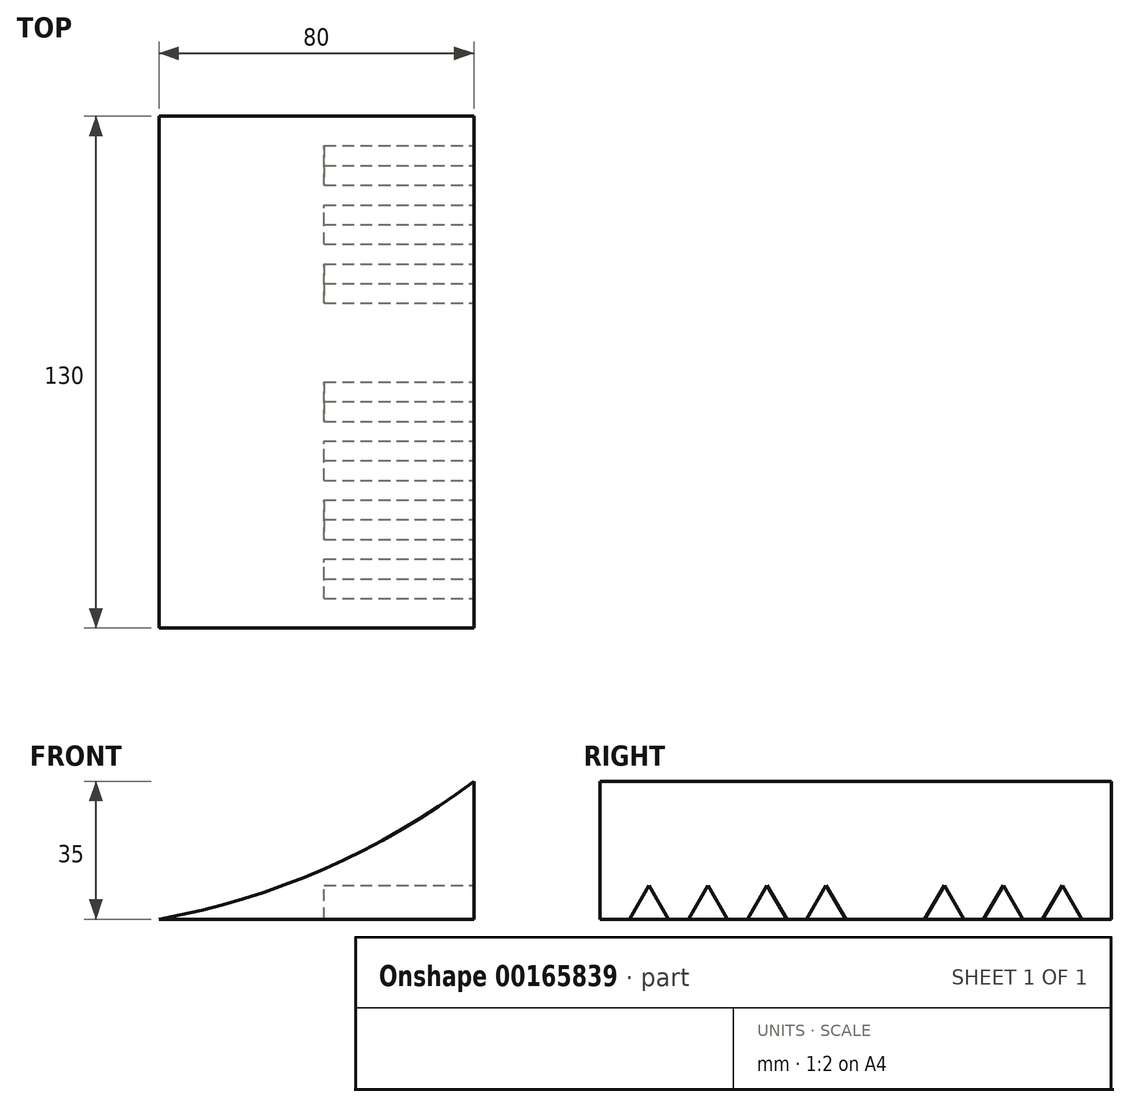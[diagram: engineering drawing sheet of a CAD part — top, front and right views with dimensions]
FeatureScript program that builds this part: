
annotation { "Feature Type Name" : "Feature", "Feature Type Description" : "" }
export const myFeature = defineFeature(function(context is Context, id is Id, definition is map)
    precondition{}
    {
        {
            var Q0;
            Q0=qCreatedBy(makeId("Front.planeOp"),FACE);
            var sketch = newSketch(context, id + "F0", { "sketchPlane" : qUnion([Q0])});
            skLineSegment(sketch, "E0", {"start": v(-40.37, -31.55) * mm, "end": v(39.63, -31.55) * mm});
            skLineSegment(sketch, "E1", {"start": v(39.63, -31.55) * mm, "end": v(39.63, 3.45) * mm});
            skArc(sketch, "E2", {"start": v(-40.37, -31.55) * mm, "mid": v(1.68, -18.73) * mm, "end": v(39.63, 3.45) * mm});
            skSolve(sketch);
        }
        {
            var Q0;
            Q0=makeQuery(id+"F0.imprint","IMPRINT",FACE,{"disambiguationData":[TD([[makeQuery(id+"F0.imprint","IMPRINT",EDGE,{"derivedFrom":sQuery(id+"F0.wireOp",EDGE,"E0")}),1.0]])]});
            extrude(context, id + "F1", {"entities" : qUnion([Q0]), "depth" : 130 * mm});
        }
        {
            var Q0;
            Q0=makeQuery(id+"F1.opExtrude","SWEPT_FACE",FACE,{"disambiguationData":[OSD([sQuery(id+"F0.wireOp",EDGE,"E1")])]});
            var sketch = newSketch(context, id + "F2", { "sketchPlane" : qUnion([Q0])});
            skLineSegment(sketch, "E3", {"start": v(-130, -31.55) * mm, "end": v(-122.5, -31.55) * mm});
            skLineSegment(sketch, "E4", {"start": v(-122.5, -31.55) * mm, "end": v(-117.5, -22.9) * mm});
            skLineSegment(sketch, "E5", {"start": v(-117.5, -22.9) * mm, "end": v(-112.5, -31.55) * mm});
            skLineSegment(sketch, "E6", {"start": v(-112.5, -31.55) * mm, "end": v(-122.5, -31.55) * mm});
            skLineSegment(sketch, "E7", {"start": v(-112.5, -31.55) * mm, "end": v(-110, -31.55) * mm, "construction": true});
            skLineSegment(sketch, "E8", {"start": v(-110, -31.55) * mm, "end": v(-110, -15) * mm, "construction": true});
            skLineSegment(sketch, "E9.MirrorCS", {"start": v(-107.5, -31.55) * mm, "end": v(-97.5, -31.55) * mm});
            skLineSegment(sketch, "E10.MirrorCS", {"start": v(-102.5, -22.9) * mm, "end": v(-107.5, -31.55) * mm});
            skLineSegment(sketch, "E11.MirrorCS", {"start": v(-97.5, -31.55) * mm, "end": v(-102.5, -22.9) * mm});
            skLineSegment(sketch, "E12", {"start": v(-97.5, -31.55) * mm, "end": v(-95, -31.55) * mm, "construction": true});
            skLineSegment(sketch, "E13", {"start": v(-95, -31.55) * mm, "end": v(-95, -11.34) * mm, "construction": true});
            skLineSegment(sketch, "E14.MirrorCS", {"start": v(-92.5, -31.55) * mm, "end": v(-87.5, -22.9) * mm});
            skLineSegment(sketch, "E15.MirrorCS", {"start": v(-82.5, -31.55) * mm, "end": v(-92.5, -31.55) * mm});
            skLineSegment(sketch, "E16.MirrorCS", {"start": v(-87.5, -22.9) * mm, "end": v(-82.5, -31.55) * mm});
            skLineSegment(sketch, "E17.MirrorCS", {"start": v(-72.5, -22.9) * mm, "end": v(-77.5, -31.55) * mm});
            skLineSegment(sketch, "E18.MirrorCS", {"start": v(-67.5, -31.55) * mm, "end": v(-72.5, -22.9) * mm});
            skLineSegment(sketch, "E19.MirrorCS", {"start": v(-77.5, -31.55) * mm, "end": v(-67.5, -31.55) * mm});
            skLineSegment(sketch, "E20", {"start": v(-67.5, -31.55) * mm, "end": v(-65, -31.55) * mm, "construction": true});
            skLineSegment(sketch, "E21", {"start": v(-65, -31.55) * mm, "end": v(-65, -10.36) * mm, "construction": true});
            skLineSegment(sketch, "E22.MirrorCS", {"start": v(-62.5, -31.55) * mm, "end": v(-57.5, -22.9) * mm});
            skLineSegment(sketch, "E23.MirrorCS", {"start": v(-52.5, -31.55) * mm, "end": v(-62.5, -31.55) * mm});
            skLineSegment(sketch, "E24.MirrorCS", {"start": v(-57.5, -22.9) * mm, "end": v(-52.5, -31.55) * mm});
            skLineSegment(sketch, "E25.MirrorCS", {"start": v(-42.5, -22.9) * mm, "end": v(-47.5, -31.55) * mm});
            skLineSegment(sketch, "E26.MirrorCS", {"start": v(-47.5, -31.55) * mm, "end": v(-37.5, -31.55) * mm});
            skLineSegment(sketch, "E27.MirrorCS", {"start": v(-37.5, -31.55) * mm, "end": v(-42.5, -22.9) * mm});
            skLineSegment(sketch, "E28.MirrorCS", {"start": v(-32.5, -31.55) * mm, "end": v(-27.5, -22.9) * mm});
            skLineSegment(sketch, "E29.MirrorCS", {"start": v(-22.5, -31.55) * mm, "end": v(-32.5, -31.55) * mm});
            skLineSegment(sketch, "E30.MirrorCS", {"start": v(-27.5, -22.9) * mm, "end": v(-22.5, -31.55) * mm});
            skLineSegment(sketch, "E31.MirrorCS", {"start": v(-17.5, -31.55) * mm, "end": v(-7.5, -31.55) * mm});
            skLineSegment(sketch, "E32.MirrorCS", {"start": v(-7.5, -31.55) * mm, "end": v(-12.5, -22.9) * mm});
            skLineSegment(sketch, "E33.MirrorCS", {"start": v(-12.5, -22.9) * mm, "end": v(-17.5, -31.55) * mm});
            skSolve(sketch);
        }
        {
            var Q0;
            Q0=makeQuery(id+"F2.imprint","IMPRINT",FACE,{"disambiguationData":[TD([[makeQuery(id+"F2.imprint","IMPRINT",EDGE,{"derivedFrom":sQuery(id+"F2.wireOp",EDGE,"E4")}),-1.0]])]});
            var Q1;
            Q1=makeQuery(id+"F2.imprint","IMPRINT",FACE,{"disambiguationData":[TD([[makeQuery(id+"F2.imprint","IMPRINT",EDGE,{"derivedFrom":sQuery(id+"F2.wireOp",EDGE,"E9.MirrorCS")}),1.0]])]});
            var Q2;
            Q2=makeQuery(id+"F2.imprint","IMPRINT",FACE,{"disambiguationData":[TD([[makeQuery(id+"F2.imprint","IMPRINT",EDGE,{"derivedFrom":sQuery(id+"F2.wireOp",EDGE,"E14.MirrorCS")}),-1.0]])]});
            var Q3;
            Q3=makeQuery(id+"F2.imprint","IMPRINT",FACE,{"disambiguationData":[TD([[makeQuery(id+"F2.imprint","IMPRINT",EDGE,{"derivedFrom":sQuery(id+"F2.wireOp",EDGE,"E17.MirrorCS")}),1.0]])]});
            var Q4;
            Q4=makeQuery(id+"F2.imprint","IMPRINT",FACE,{"disambiguationData":[TD([[makeQuery(id+"F2.imprint","IMPRINT",EDGE,{"derivedFrom":sQuery(id+"F2.wireOp",EDGE,"E22.MirrorCS")}),-1.0]])]});
            var Q5;
            Q5=makeQuery(id+"F2.imprint","IMPRINT",FACE,{"disambiguationData":[TD([[makeQuery(id+"F2.imprint","IMPRINT",EDGE,{"derivedFrom":sQuery(id+"F2.wireOp",EDGE,"E26.MirrorCS")}),1.0]])]});
            var Q6;
            Q6=makeQuery(id+"F2.imprint","IMPRINT",FACE,{"disambiguationData":[TD([[makeQuery(id+"F2.imprint","IMPRINT",EDGE,{"derivedFrom":sQuery(id+"F2.wireOp",EDGE,"E28.MirrorCS")}),-1.0]])]});
            var Q7;
            Q7=makeQuery(id+"F2.imprint","IMPRINT",FACE,{"disambiguationData":[TD([[makeQuery(id+"F2.imprint","IMPRINT",EDGE,{"derivedFrom":sQuery(id+"F2.wireOp",EDGE,"E31.MirrorCS")}),1.0]])]});
            extrude(context, id + "F3", {"entities" : qUnion([Q0, Q1, Q2, Q3, Q4, Q5, Q6, Q7]), "operationType" : NewBodyOperationType.REMOVE, "oppositeDirection" : true, "depth" : 38 * mm});
        }
    });
